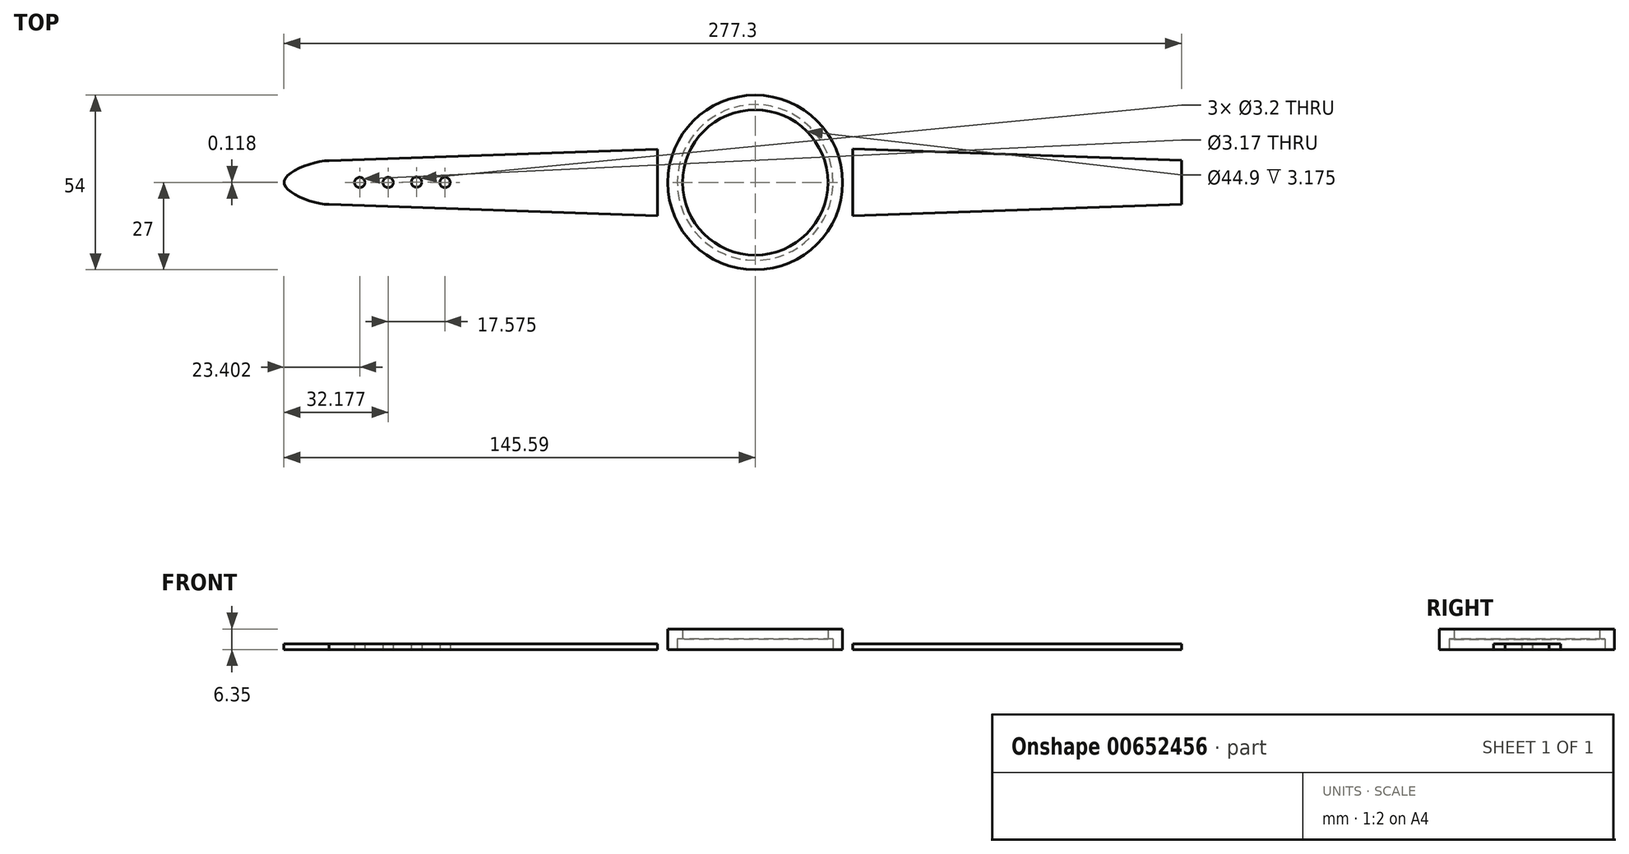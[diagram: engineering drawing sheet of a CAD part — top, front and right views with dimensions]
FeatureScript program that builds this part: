
annotation { "Feature Type Name" : "Feature", "Feature Type Description" : "" }
export const myFeature = defineFeature(function(context is Context, id is Id, definition is map)
    precondition{}
    {
        {
            var Q0;
            Q0=qCreatedBy(makeId("Top.planeOp"),FACE);
            var sketch = newSketch(context, id + "F0", { "sketchPlane" : qUnion([Q0])});
            skCircle(sketch, "E0", {"center": v(0, 0) * mm, "radius": 27 * mm});
            skCircle(sketch, "E1", {"center": v(0, 0) * mm, "radius": 22.45 * mm});
            skLineSegment(sketch, "E2", {"start": v(-30.18, 10.33) * mm, "end": v(-30.18, -10.31) * mm});
            skLineSegment(sketch, "E3", {"start": v(-30.17, 10.33) * mm, "end": v(-131.71, 6.78) * mm});
            skLineSegment(sketch, "E4", {"start": v(-30.17, -10.31) * mm, "end": v(-131.71, -6.77) * mm});
            skLineSegment(sketch, "E5", {"start": v(-131.71, 6.78) * mm, "end": v(-131.71, -6.77) * mm});
            skLineSegment(sketch, "E6", {"start": v(30.18, 10.34) * mm, "end": v(30.18, -10.3) * mm});
            skLineSegment(sketch, "E7", {"start": v(30.17, 10.34) * mm, "end": v(131.71, 6.8) * mm});
            skLineSegment(sketch, "E8", {"start": v(30.17, -10.3) * mm, "end": v(131.71, -6.75) * mm});
            skLineSegment(sketch, "E9", {"start": v(131.71, 6.8) * mm, "end": v(131.71, -6.75) * mm});
            skCircle(sketch, "E10", {"center": v(-122.19, 0) * mm, "radius": 1.59 * mm});
            skPoint(sketch, "E10.first.point", {"position": v(-120.6, 0.05) * mm});
            skPoint(sketch, "E10.second.point", {"position": v(-120.6, -0.06) * mm});
            skPoint(sketch, "E10.third.point", {"position": v(-120.6, 0) * mm});
            skCircle(sketch, "E11", {"center": v(-113.41, 0) * mm, "radius": 1.6 * mm});
            skCircle(sketch, "E12", {"center": v(-104.63, 0.12) * mm, "radius": 1.6 * mm});
            skCircle(sketch, "E13", {"center": v(-95.84, 0) * mm, "radius": 1.6 * mm});
            skFitSpline(sketch, "E14", {"points": [v(-131.71, 6.78) * mm, v(-145.59, 0) * mm, v(-131.71, -6.77) * mm], "startDerivative": vector(-29.66, -1.11) * mm, "endDerivative": vector(28.5, 0) * mm});
            skSolve(sketch);
        }
        {
            var Q0;
            Q0=makeQuery(id+"F0.imprint","IMPRINT",FACE,{"disambiguationData":[TD([[makeQuery(id+"F0.imprint","IMPRINT",EDGE,{"derivedFrom":sQuery(id+"F0.wireOp",EDGE,"E1")}),1.0]])]});
            var Q1;
            Q1=makeQuery(id+"F0.imprint","IMPRINT",FACE,{"disambiguationData":[TD([[makeQuery(id+"F0.imprint","IMPRINT",EDGE,{"derivedFrom":sQuery(id+"F0.wireOp",EDGE,"E0")}),1.0]])]});
            extrude(context, id + "F1", {"entities" : qUnion([Q0, Q1]), "depth" : 3.17 * mm, "offsetDistance" : 25.4 * mm});
        }
        {
            var Q0;
            Q0=makeQuery(id+"F0.imprint","IMPRINT",FACE,{"disambiguationData":[TD([[makeQuery(id+"F0.imprint","IMPRINT",EDGE,{"derivedFrom":sQuery(id+"F0.wireOp",EDGE,"E0")}),1.0]])]});
            extrude(context, id + "F2", {"entities" : qUnion([Q0]), "operationType" : NewBodyOperationType.ADD, "depth" : 6.35 * mm, "offsetDistance" : 25.4 * mm});
        }
        {
            var Q0;
            Q0=makeQuery(id+"F0.imprint","IMPRINT",FACE,{"disambiguationData":[TD([[makeQuery(id+"F0.imprint","IMPRINT",EDGE,{"derivedFrom":sQuery(id+"F0.wireOp",EDGE,"E2")}),-1.0]])]});
            var Q1;
            Q1=makeQuery(id+"F0.imprint","IMPRINT",FACE,{"disambiguationData":[TD([[makeQuery(id+"F0.imprint","IMPRINT",EDGE,{"derivedFrom":sQuery(id+"F0.wireOp",EDGE,"E6")}),1.0]])]});
            var Q2;
            Q2=makeQuery(id+"F0.imprint","IMPRINT",FACE,{"disambiguationData":[TD([[makeQuery(id+"F0.imprint","IMPRINT",EDGE,{"derivedFrom":sQuery(id+"F0.wireOp",EDGE,"E5")}),-1.0]])]});
            extrude(context, id + "F3", {"entities" : qUnion([Q0, Q1, Q2]), "depth" : 1.78 * mm, "offsetDistance" : 25.4 * mm});
        }
        {
            var Q0;
            Q0=qCreatedBy(makeId("Top.planeOp"),FACE);
            var sketch = newSketch(context, id + "F4", { "sketchPlane" : qUnion([Q0])});
            skCircle(sketch, "E15", {"center": v(0, 0) * mm, "radius": 24.07 * mm});
            skSolve(sketch);
        }
        {
            var Q0;
            Q0 = qSketchRegion(id + "F4", true);
            extrude(context, id + "F5", {"entities" : qUnion([Q0]), "operationType" : NewBodyOperationType.ADD, "depth" : 3.17 * mm, "offsetDistance" : 25.4 * mm});
        }
        {
            var Q0;
            Q0=makeQuery(id+"F4.imprint","IMPRINT",FACE,{"disambiguationData":[TD([[makeQuery(id+"F4.imprint","IMPRINT",EDGE,{"derivedFrom":sQuery(id+"F4.wireOp",EDGE,"E15")}),1.0]])]});
            extrude(context, id + "F6", {"entities" : qUnion([Q0]), "depth" : 3.25 * mm, "offsetDistance" : 25.4 * mm});
        }
    });
